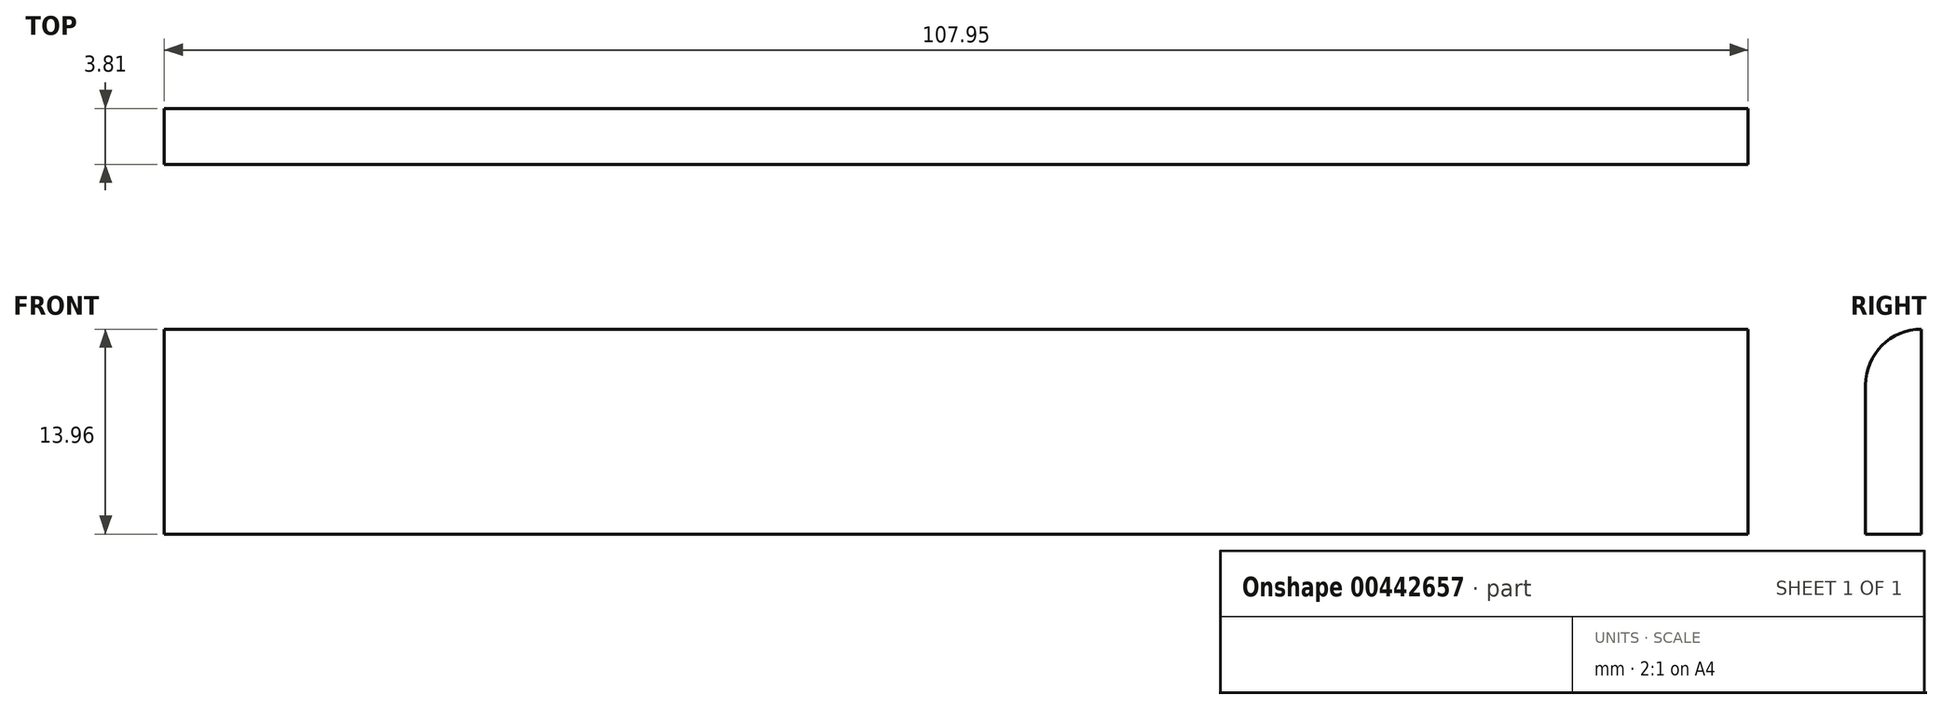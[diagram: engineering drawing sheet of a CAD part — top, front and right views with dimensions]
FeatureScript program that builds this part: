
annotation { "Feature Type Name" : "Feature", "Feature Type Description" : "" }
export const myFeature = defineFeature(function(context is Context, id is Id, definition is map)
    precondition{}
    {
        {
            var Q0;
            Q0=qCreatedBy(makeId("Right.planeOp"),FACE);
            var sketch = newSketch(context, id + "F0", { "sketchPlane" : qUnion([Q0])});
            skLineSegment(sketch, "E0", {"start": v(0, 0) * mm, "end": v(0, 10.16) * mm});
            skPoint(sketch, "E1.end.orphan", {"position": v(3.08, 9.28) * mm});
            skPoint(sketch, "E2.start.orphan", {"position": v(3.08, 13.9) * mm});
            skArc(sketch, "E3", {"start": v(3.8, 13.96) * mm, "mid": v(1.11, 12.84) * mm, "end": v(0, 10.14) * mm});
            skPoint(sketch, "E3.second.point", {"position": v(7.62, 10.16) * mm});
            skPoint(sketch, "E3.third.point", {"position": v(3.4, 6.36) * mm});
            skLineSegment(sketch, "E4", {"start": v(0, 0) * mm, "end": v(3.81, 0) * mm});
            skLineSegment(sketch, "E5", {"start": v(3.81, 0) * mm, "end": v(3.8, 13.96) * mm});
            skPoint(sketch, "E6.orphan", {"position": v(3.8, 17) * mm});
            skSolve(sketch);
        }
        {
            var Q0;
            {var subQ0=sQuery(id+"F0.wireOp",EDGE,"E0");Q0=makeQuery(id+"F0.imprint","IMPRINT",FACE,{"disambiguationData":[TD([[makeQuery(id+"F0.imprint","IMPRINT",EDGE,{"derivedFrom":subQ0}),-1.0]])]});}
            extrude(context, id + "F1", {"entities" : qUnion([Q0]), "depth" : 107.95 * mm});
        }
    });
